# Revit family: LeL Metope 1.1
name_source: partatom
category: Lighting Fixtures
units: mm (PartAtom-declared; Revit-internal decimal feet)

## family parameters
Cut with Voids When Loaded = Yes
Host = Face
Light Source = No
Part Type = Normal
Room Calculation Point = No
Round Connector Dimension = Use Diameter
Shared = No

## types (4) — shared parameters
Alimentazione = 24 V
Apparent Load = 3 VA
CCT = 3000 K
CRI = 80
Default Elevation = 1219 mm
Description = Outdoor Wall Mounted
Height = 60 mm  [stored 0.19685 ft]
IK = IK05
IP = IP65
Lamp = LED
Lenght = 35 mm  [stored 0.114829 ft]
Manufacturer = L&L Luce&Light
Model = TM11
Rated Power supply = 24 V
URL = https://www.lucelight.it
Wattage = 3 W
Weight = 0.15 kg
Widht = 15 mm  [stored 0.0492126 ft]

## per-type parameters (varying)
| type | Lumen Output | Photometry2 |
| 1.1 D 3W 24Vdc | 104 lm | TM1 Light source : 1.1 D 3W 24Vdc |
| 1.1 L 36° 3W 24Vdc | 108 lm | TM1 Light source : 1.1 L 36° 3W 24Vdc |
| 1.1 M 22° 3W 24Vdc | 116 lm | TM1 Light source : 1.1 M 22° 3W 24Vdc |
| 1.1 S 17° 3W 24Vdc | 153 lm | TM1 Light source : 1.1 S 17° 3W 24Vdc |

note: [stored X ft] marks values corroborated as IEEE doubles in the binary element streams (Revit-internal decimal feet)
